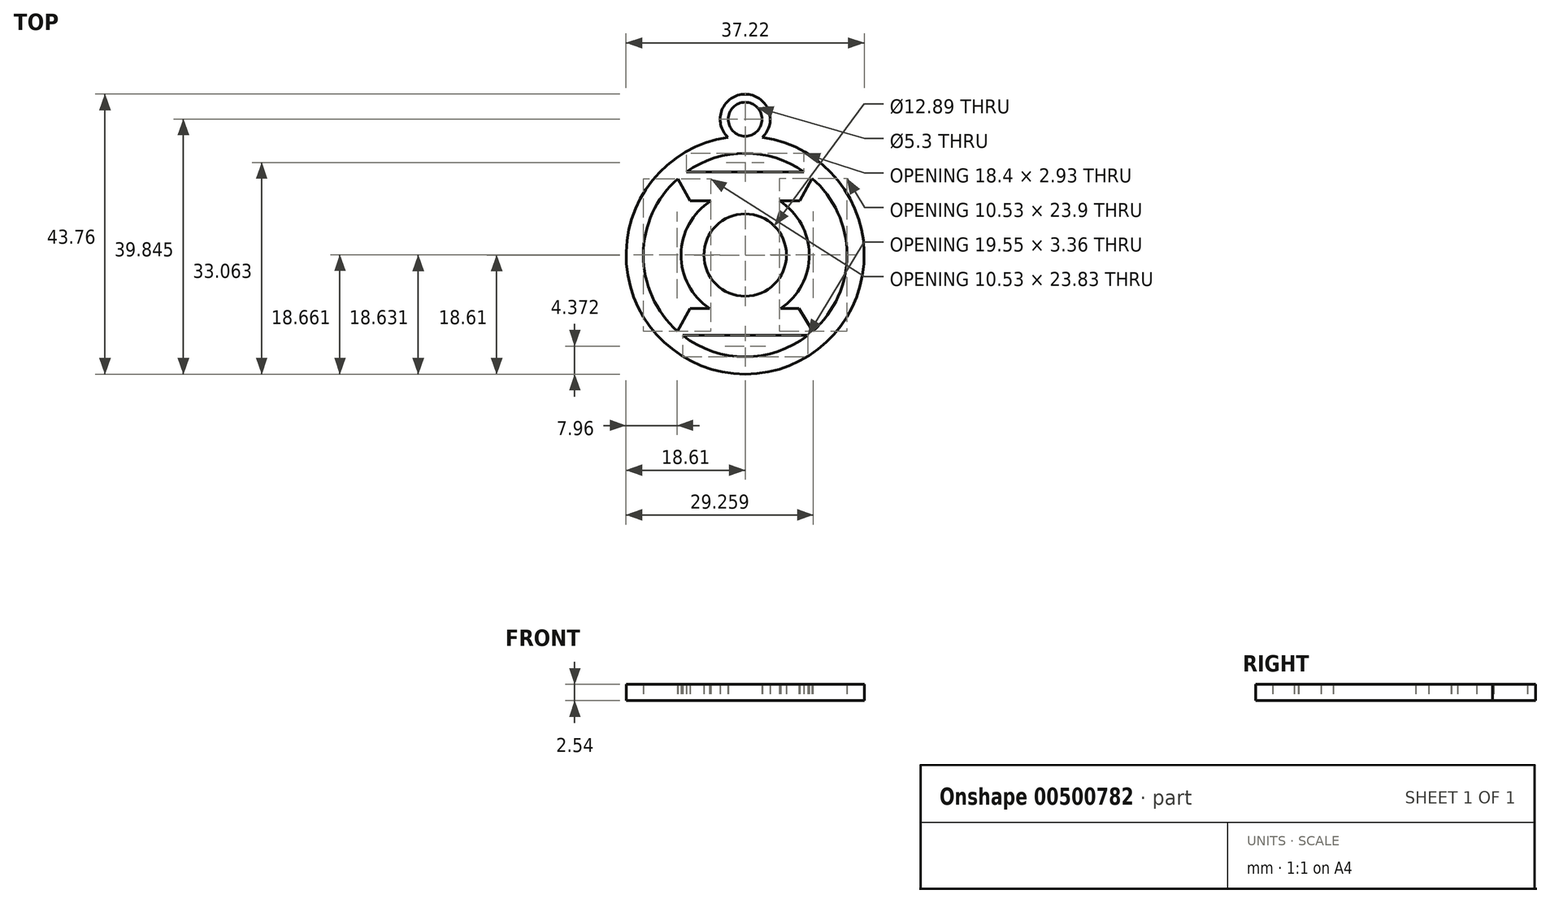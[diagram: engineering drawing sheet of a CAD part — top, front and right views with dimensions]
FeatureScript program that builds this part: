
annotation { "Feature Type Name" : "Feature", "Feature Type Description" : "" }
export const myFeature = defineFeature(function(context is Context, id is Id, definition is map)
    precondition{}
    {
        {
            var Q0;
            Q0=qCreatedBy(makeId("Top.planeOp"),FACE);
            var sketch = newSketch(context, id + "F0", { "sketchPlane" : qUnion([Q0])});
            skPoint(sketch, "E0.middle", {"position": v(0, 0) * mm});
            skCircle(sketch, "E1", {"center": v(0, 0) * mm, "radius": 6.44 * mm});
            skArc(sketch, "E2", {"start": v(9.2, 12.99) * mm, "mid": v(0, 15.92) * mm, "end": v(-9.2, 12.99) * mm});
            skLineSegment(sketch, "E3", {"start": v(-9.2, 12.99) * mm, "end": v(9.2, 12.99) * mm});
            skLineSegment(sketch, "E4", {"start": v(-10.53, 11.94) * mm, "end": v(-8.63, 8.45) * mm});
            skLineSegment(sketch, "E5", {"start": v(-8.63, 8.45) * mm, "end": v(-5.38, 8.45) * mm});
            skLineSegment(sketch, "E6", {"start": v(8.5, 8.45) * mm, "end": v(10.46, 12) * mm});
            skArc(sketch, "E7", {"start": v(-5.38, 8.45) * mm, "mid": v(-10.02, 0.1) * mm, "end": v(-5.54, -8.34) * mm});
            skLineSegment(sketch, "E8", {"start": v(-10.58, -11.9) * mm, "end": v(-8.63, -8.34) * mm});
            skLineSegment(sketch, "E9", {"start": v(-8.63, -8.34) * mm, "end": v(-5.54, -8.34) * mm});
            skLineSegment(sketch, "E10", {"start": v(8.4, -8.34) * mm, "end": v(10.57, -11.9) * mm});
            skLineSegment(sketch, "E11", {"start": v(-9.78, -12.56) * mm, "end": v(9.78, -12.56) * mm});
            skPoint(sketch, "E0.top.start.orphan", {"position": v(18.86, 18.86) * mm});
            skPoint(sketch, "E0.right.end.orphan", {"position": v(-18.86, 18.86) * mm});
            skPoint(sketch, "E0.bottom.end.orphan", {"position": v(-18.86, -18.86) * mm});
            skPoint(sketch, "E0.bottom.start.orphan", {"position": v(18.86, -18.86) * mm});
            skArc(sketch, "E12.trimOffspring", {"start": v(-10.53, 11.94) * mm, "mid": v(-15.92, 0.03) * mm, "end": v(-10.58, -11.9) * mm});
            skLineSegment(sketch, "E13.trimOffspring", {"start": v(5.38, 8.45) * mm, "end": v(8.5, 8.45) * mm});
            skArc(sketch, "E14.trimOffspring", {"start": v(-9.78, -12.56) * mm, "mid": v(0, -15.92) * mm, "end": v(9.78, -12.56) * mm});
            skArc(sketch, "E15.trimOffspring", {"start": v(10.57, -11.9) * mm, "mid": v(15.92, 0.08) * mm, "end": v(10.46, 12) * mm});
            skLineSegment(sketch, "E16.trimOffspring", {"start": v(5.54, -8.34) * mm, "end": v(8.4, -8.34) * mm});
            skArc(sketch, "E17.trimOffspring", {"start": v(5.54, -8.34) * mm, "mid": v(10.02, 0.1) * mm, "end": v(5.38, 8.45) * mm});
            skArc(sketch, "E18", {"start": v(2.7, 18.4) * mm, "mid": v(0, 25.15) * mm, "end": v(-2.7, 18.4) * mm});
            skCircle(sketch, "E19", {"center": v(0, 21.24) * mm, "radius": 2.65 * mm});
            skArc(sketch, "E20.trimOffspring", {"start": v(-2.7, 18.4) * mm, "mid": v(0, -18.6) * mm, "end": v(2.7, 18.4) * mm});
            skSolve(sketch);
        }
        {
            var Q0;
            Q0 = qSketchRegion(id + "F0", true);
            extrude(context, id + "F1", {"entities" : qUnion([Q0]), "depth" : 2.54 * mm});
        }
    });
